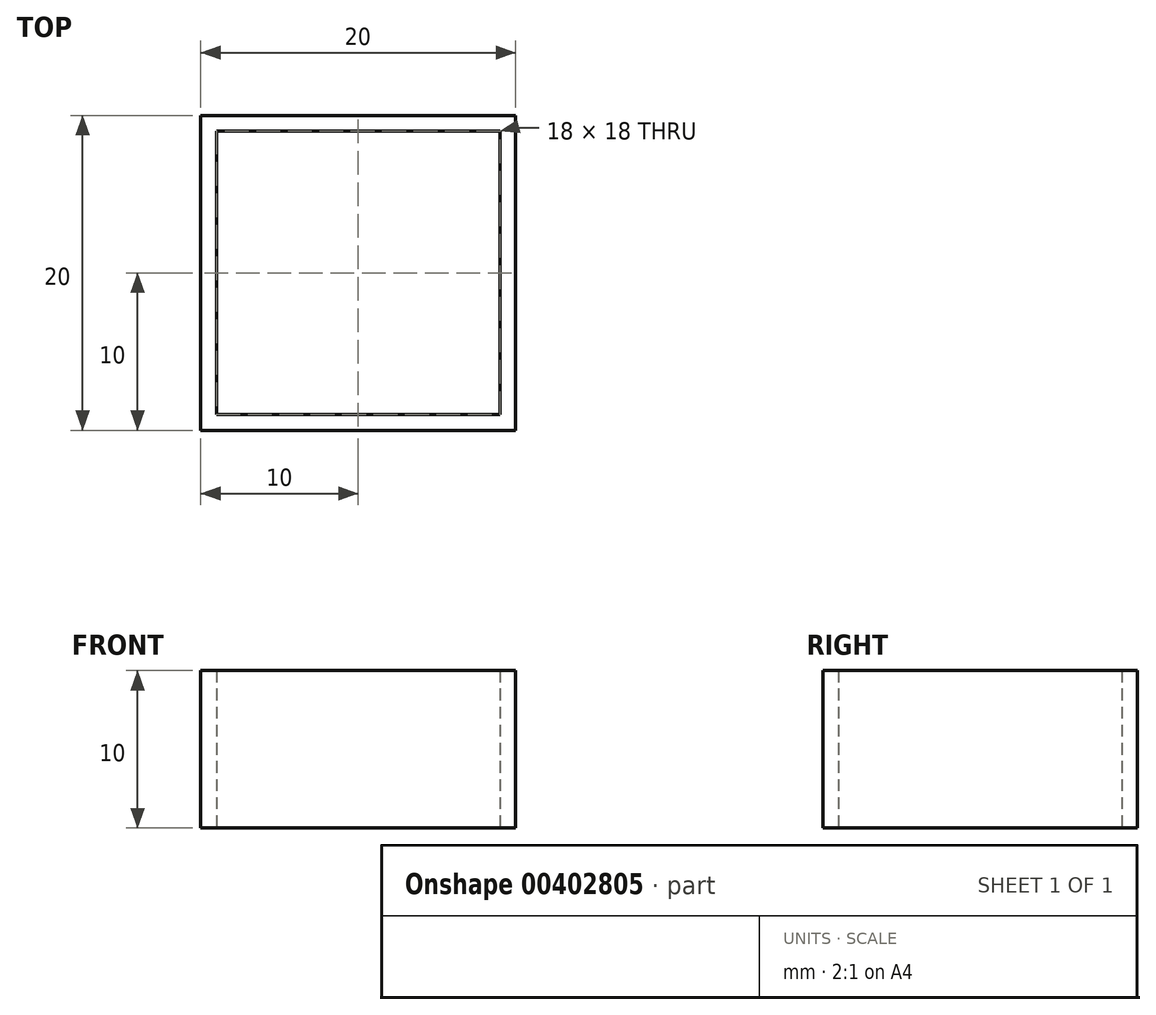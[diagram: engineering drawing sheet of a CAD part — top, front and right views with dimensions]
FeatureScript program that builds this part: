
annotation { "Feature Type Name" : "Feature", "Feature Type Description" : "" }
export const myFeature = defineFeature(function(context is Context, id is Id, definition is map)
    precondition{}
    {
        {
            var Q0;
            Q0=qCreatedBy(makeId("Top.planeOp"),FACE);
            var sketch = newSketch(context, id + "F0", { "sketchPlane" : qUnion([Q0])});
            skLineSegment(sketch, "E0.bottom", {"start": v(10, 10) * mm, "end": v(-10, 10) * mm});
            skLineSegment(sketch, "E0.top", {"start": v(10, -10) * mm, "end": v(-10, -10) * mm});
            skLineSegment(sketch, "E0.left", {"start": v(10, 10) * mm, "end": v(10, -10) * mm});
            skLineSegment(sketch, "E0.right", {"start": v(-10, 10) * mm, "end": v(-10, -10) * mm});
            skPoint(sketch, "E0.middle", {"position": v(0, 0) * mm});
            skLineSegment(sketch, "E1.0", {"start": v(9, 9) * mm, "end": v(-9, 9) * mm});
            skLineSegment(sketch, "E1.1", {"start": v(9, 9) * mm, "end": v(9, -9) * mm});
            skLineSegment(sketch, "E1.2", {"start": v(9, -9) * mm, "end": v(-9, -9) * mm});
            skLineSegment(sketch, "E1.3", {"start": v(-9, 9) * mm, "end": v(-9, -9) * mm});
            skSolve(sketch);
        }
        {
            var Q0;
            Q0=makeQuery(id+"F0.imprint","IMPRINT",FACE,{"disambiguationData":[TD([[makeQuery(id+"F0.imprint","IMPRINT",EDGE,{"derivedFrom":sQuery(id+"F0.wireOp",EDGE,"E0.bottom")}),1.0]])]});
            extrude(context, id + "F1", {"entities" : qUnion([Q0]), "depth" : 10 * mm});
        }
    });
